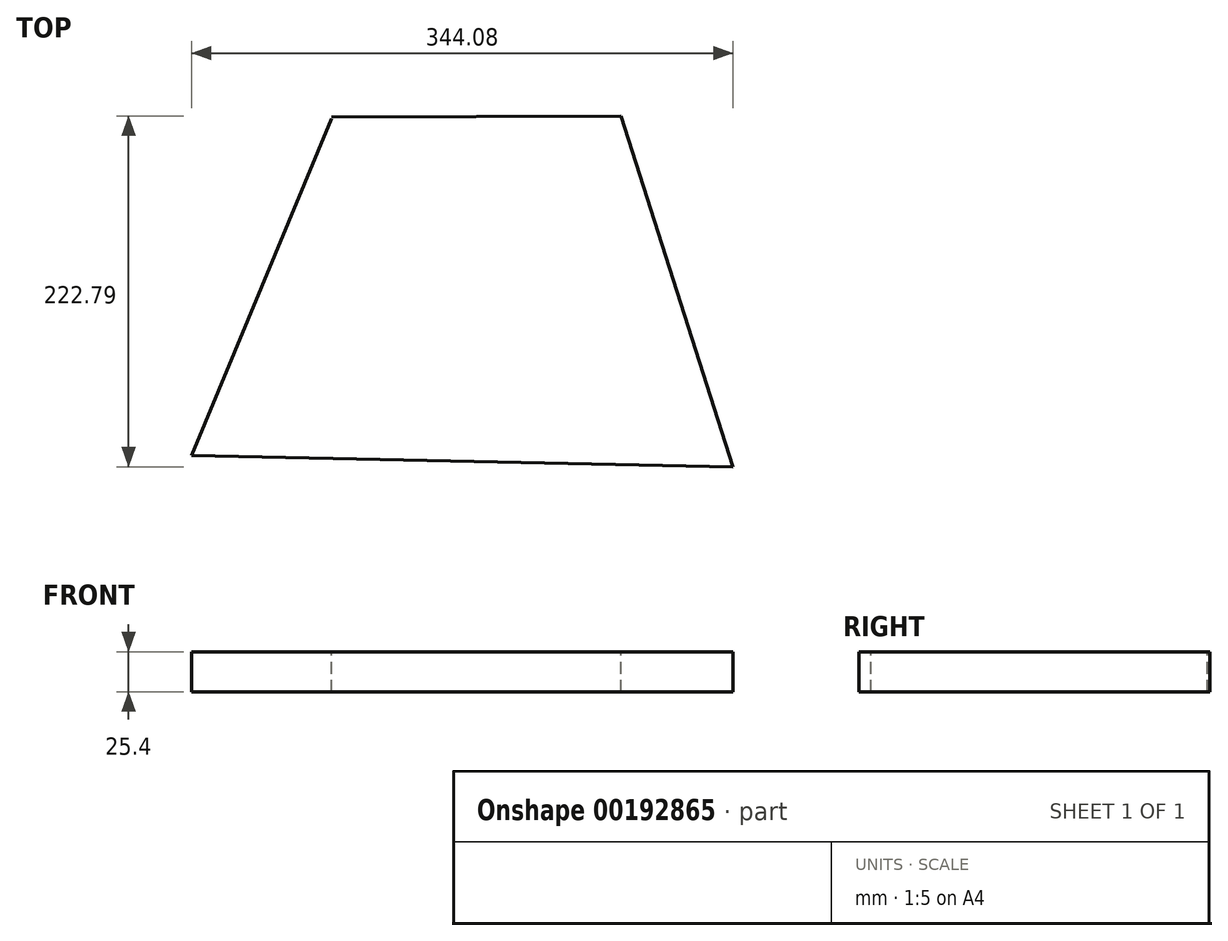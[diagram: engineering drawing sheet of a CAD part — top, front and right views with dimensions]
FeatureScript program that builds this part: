
annotation { "Feature Type Name" : "Feature", "Feature Type Description" : "" }
export const myFeature = defineFeature(function(context is Context, id is Id, definition is map)
    precondition{}
    {
        {
            var Q0;
            Q0=qCreatedBy(makeId("Top.planeOp"),FACE);
            var sketch = newSketch(context, id + "F0", { "sketchPlane" : qUnion([Q0])});
            skLineSegment(sketch, "E0", {"start": v(-86.31, 96.73) * mm, "end": v(97.5, 97.47) * mm});
            skLineSegment(sketch, "E1", {"start": v(97.5, 97.47) * mm, "end": v(168.81, -125.32) * mm});
            skLineSegment(sketch, "E2", {"start": v(168.81, -125.32) * mm, "end": v(-175.27, -117.97) * mm});
            skLineSegment(sketch, "E3", {"start": v(-175.27, -117.97) * mm, "end": v(-86.31, 96) * mm});
            skSolve(sketch);
        }
        {
            var Q0;
            Q0=sQuery(id+"F0.wireOp",EDGE,"E0");
            var Q1;
            Q1=sQuery(id+"F0.wireOp",EDGE,"E1");
            var Q2;
            Q2=sQuery(id+"F0.wireOp",EDGE,"E2");
            var Q3;
            Q3=sQuery(id+"F0.wireOp",EDGE,"E3");
            extrude(context, id + "F1", {"bodyType" : ToolBodyType.SURFACE, "surfaceEntities" : qUnion([Q0, Q1, Q2, Q3]), "depth" : 25.4 * mm});
        }
    });
